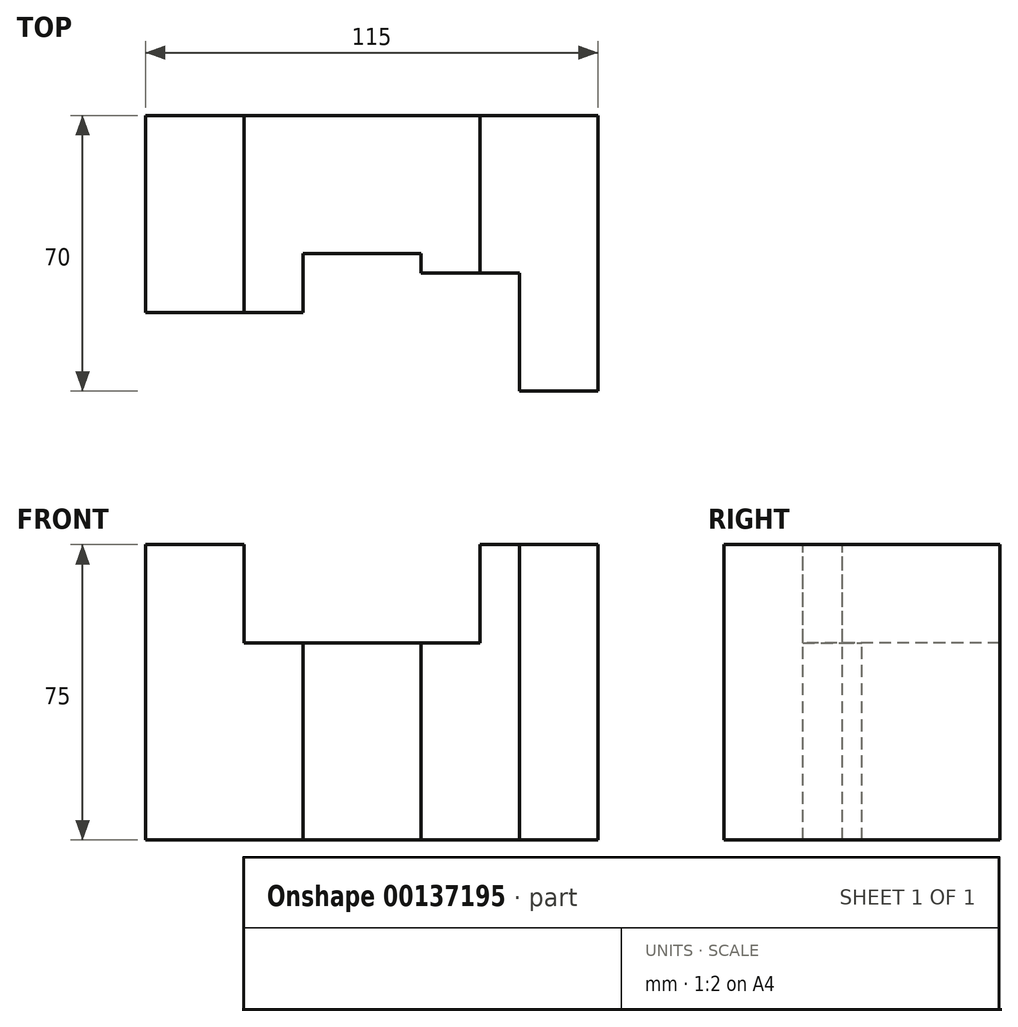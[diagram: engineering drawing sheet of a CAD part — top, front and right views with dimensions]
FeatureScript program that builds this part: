
annotation { "Feature Type Name" : "Feature", "Feature Type Description" : "" }
export const myFeature = defineFeature(function(context is Context, id is Id, definition is map)
    precondition{}
    {
        {
            var Q0;
            Q0=qCreatedBy(makeId("Front.planeOp"),FACE);
            var sketch = newSketch(context, id + "F0", { "sketchPlane" : qUnion([Q0])});
            skLineSegment(sketch, "E0.bottom", {"start": v(0, 0) * mm, "end": v(115, 0) * mm});
            skLineSegment(sketch, "E0.top", {"start": v(0, 75) * mm, "end": v(115, 75) * mm});
            skLineSegment(sketch, "E0.left", {"start": v(0, 0) * mm, "end": v(0, 75) * mm});
            skLineSegment(sketch, "E0.right", {"start": v(115, 0) * mm, "end": v(115, 75) * mm});
            skSolve(sketch);
        }
        {
            var Q0;
            Q0 = qSketchRegion(id + "F0", true);
            extrude(context, id + "F1", {"entities" : qUnion([Q0]), "depth" : 70 * mm});
        }
        {
            var Q0;
            Q0=makeQuery(id+"F1.opExtrude","CAP_FACE",FACE,{"disambiguationData":[OSD([sQuery(id+"F0.wireOp",EDGE,"E0.bottom"),sQuery(id+"F0.wireOp",EDGE,"E0.top"),sQuery(id+"F0.wireOp",EDGE,"E0.left"),sQuery(id+"F0.wireOp",EDGE,"E0.right")])],"isStart":false});
            var sketch = newSketch(context, id + "F2", { "sketchPlane" : qUnion([Q0])});
            skLineSegment(sketch, "E1.bottom", {"start": v(25, 75) * mm, "end": v(85, 75) * mm});
            skLineSegment(sketch, "E1.top", {"start": v(25, 50) * mm, "end": v(85, 50) * mm});
            skLineSegment(sketch, "E1.left", {"start": v(25, 75) * mm, "end": v(25, 50) * mm});
            skLineSegment(sketch, "E1.right", {"start": v(85, 75) * mm, "end": v(85, 50) * mm});
            skSolve(sketch);
        }
        {
            var Q0;
            Q0 = qSketchRegion(id + "F2", true);
            extrude(context, id + "F3", {"entities" : qUnion([Q0]), "operationType" : NewBodyOperationType.REMOVE, "oppositeDirection" : true, "depth" : 70 * mm});
        }
        {
            var Q0;
            {var subQ0=sQuery(id+"F0.wireOp",EDGE,"E0.right");var subQ2=sQuery(id+"F0.wireOp",EDGE,"E0.top");Q0=makeQuery(id+"F3.boolean.opBoolean","SPLIT",FACE,{"disambiguationData":[TD([makeQuery(id+"F1.opExtrude","SWEPT_FACE",FACE,{"disambiguationData":[OSD([subQ0])]})])],"derivedFrom":makeQuery(id+"F1.opExtrude","SWEPT_FACE",FACE,{"disambiguationData":[OSD([subQ2])]})});}
            var sketch = newSketch(context, id + "F4", { "sketchPlane" : qUnion([Q0])});
            skLineSegment(sketch, "E2.bottom", {"start": v(85, -70) * mm, "end": v(95, -70) * mm});
            skLineSegment(sketch, "E2.top", {"start": v(85, -40) * mm, "end": v(95, -40) * mm});
            skLineSegment(sketch, "E2.left", {"start": v(85, -70) * mm, "end": v(85, -40) * mm});
            skLineSegment(sketch, "E2.right", {"start": v(95, -70) * mm, "end": v(95, -40) * mm});
            skSolve(sketch);
        }
        {
            var Q0;
            Q0 = qSketchRegion(id + "F4", true);
            extrude(context, id + "F5", {"entities" : qUnion([Q0]), "operationType" : NewBodyOperationType.REMOVE, "oppositeDirection" : true, "depth" : 75 * mm});
        }
        {
            var Q0;
            Q0=makeQuery(id+"F3.boolean.opBoolean","COPY",FACE,{"derivedFrom":makeQuery(id+"F3.opExtrude","SWEPT_FACE",FACE,{"disambiguationData":[OSD([sQuery(id+"F2.wireOp",EDGE,"E1.top")])]})});
            var sketch = newSketch(context, id + "F6", { "sketchPlane" : qUnion([Q0])});
            skLineSegment(sketch, "E3.bottom", {"start": v(85, -40) * mm, "end": v(40, -40) * mm});
            skLineSegment(sketch, "E3.top", {"start": v(85, -70) * mm, "end": v(40, -70) * mm});
            skLineSegment(sketch, "E3.left", {"start": v(85, -40) * mm, "end": v(85, -70) * mm});
            skLineSegment(sketch, "E3.right", {"start": v(40, -40) * mm, "end": v(40, -70) * mm});
            skLineSegment(sketch, "E4.bottom", {"start": v(25, -70) * mm, "end": v(40, -70) * mm});
            skLineSegment(sketch, "E4.top", {"start": v(25, -50) * mm, "end": v(40, -50) * mm});
            skLineSegment(sketch, "E4.left", {"start": v(25, -70) * mm, "end": v(25, -50) * mm});
            skLineSegment(sketch, "E4.right", {"start": v(40, -70) * mm, "end": v(40, -50) * mm});
            skLineSegment(sketch, "E5.bottom", {"start": v(40, -40) * mm, "end": v(70, -40) * mm});
            skLineSegment(sketch, "E5.top", {"start": v(40, -35) * mm, "end": v(70, -35) * mm});
            skLineSegment(sketch, "E5.left", {"start": v(40, -40) * mm, "end": v(40, -35) * mm});
            skLineSegment(sketch, "E5.right", {"start": v(70, -40) * mm, "end": v(70, -35) * mm});
            skSolve(sketch);
        }
        {
            var Q0;
            Q0 = qSketchRegion(id + "F6", true);
            extrude(context, id + "F7", {"entities" : qUnion([Q0]), "operationType" : NewBodyOperationType.REMOVE, "oppositeDirection" : true, "depth" : 50 * mm});
        }
        {
            var Q0;
            {var subQ1=sQuery(id+"F0.wireOp",EDGE,"E0.left");var subQ2=sQuery(id+"F0.wireOp",EDGE,"E0.top");Q0=makeQuery(id+"F3.boolean.opBoolean","SPLIT",FACE,{"disambiguationData":[TD([makeQuery(id+"F1.opExtrude","SWEPT_FACE",FACE,{"disambiguationData":[OSD([subQ1])]})])],"derivedFrom":makeQuery(id+"F1.opExtrude","SWEPT_FACE",FACE,{"disambiguationData":[OSD([subQ2])]})});}
            var sketch = newSketch(context, id + "F8", { "sketchPlane" : qUnion([Q0])});
            skLineSegment(sketch, "E6.bottom", {"start": v(25, -50) * mm, "end": v(0, -50) * mm});
            skLineSegment(sketch, "E6.top", {"start": v(25, -70) * mm, "end": v(0, -70) * mm});
            skLineSegment(sketch, "E6.left", {"start": v(25, -50) * mm, "end": v(25, -70) * mm});
            skLineSegment(sketch, "E6.right", {"start": v(0, -50) * mm, "end": v(0, -70) * mm});
            skSolve(sketch);
        }
        {
            var Q0;
            Q0 = qSketchRegion(id + "F8", true);
            extrude(context, id + "F9", {"entities" : qUnion([Q0]), "operationType" : NewBodyOperationType.REMOVE, "oppositeDirection" : true, "depth" : 75 * mm});
        }
    });
